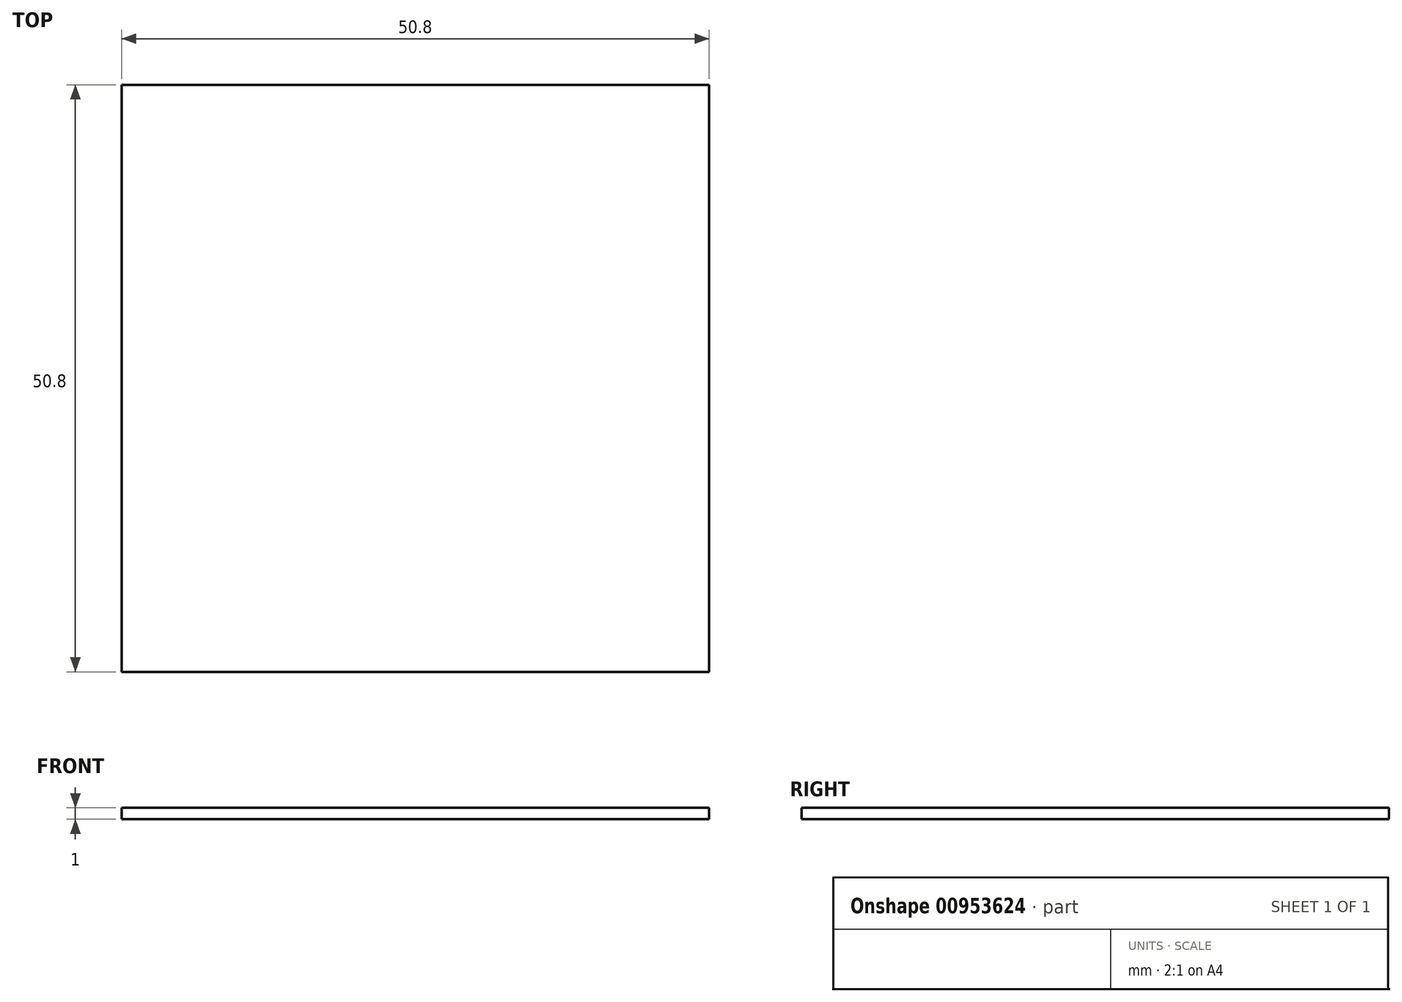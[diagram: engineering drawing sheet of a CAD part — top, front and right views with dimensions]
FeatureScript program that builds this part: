
annotation { "Feature Type Name" : "Feature", "Feature Type Description" : "" }
export const myFeature = defineFeature(function(context is Context, id is Id, definition is map)
    precondition{}
    {
        {
            var Q0;
            Q0=qCreatedBy(makeId("Top.planeOp"),FACE);
            var sketch = newSketch(context, id + "F0", { "sketchPlane" : qUnion([Q0])});
            skLineSegment(sketch, "E0.bottom", {"start": v(25.4, -25.4) * mm, "end": v(-25.4, -25.4) * mm});
            skLineSegment(sketch, "E0.top", {"start": v(25.4, 25.4) * mm, "end": v(-25.4, 25.4) * mm});
            skLineSegment(sketch, "E0.left", {"start": v(25.4, -25.4) * mm, "end": v(25.4, 25.4) * mm});
            skLineSegment(sketch, "E0.right", {"start": v(-25.4, -25.4) * mm, "end": v(-25.4, 25.4) * mm});
            skPoint(sketch, "E0.middle", {"position": v(0, 0) * mm});
            skSolve(sketch);
        }
        {
            var Q0;
            Q0=makeQuery(id+"F0.imprint","IMPRINT",FACE,{"disambiguationData":[TD([[makeQuery(id+"F0.imprint","IMPRINT",EDGE,{"derivedFrom":sQuery(id+"F0.wireOp",EDGE,"E0.bottom")}),-1.0]])]});
            extrude(context, id + "F1", {"entities" : qUnion([Q0]), "depth" : 1 * mm, "offsetDistance" : 25.4 * mm});
        }
    });
